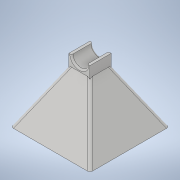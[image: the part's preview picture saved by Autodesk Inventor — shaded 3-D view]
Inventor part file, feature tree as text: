
AUTODESK INVENTOR PART (.ipt)
format: ipt  version: 2022.1 (Build 261234020, 234B)  size: 131,072 bytes
history: native  units: in
note: dims shown in document units (in); Inventor stores cm internally (conversion verified against a paired STEP export)
features: sketch x3, plane x2, fillet x2, loft x1, extrude x1
ambient origin geometry x8: Origin, YZ Plane, XZ Plane, XY Plane, X Axis, Y Axis, Z Axis, Center Point
bodies: Solid1 (feature_tree)
feature tree (9):
  sketch  "Sketch1"  dims[d3=0.0in d4=90.0deg d5=0.0in d6=90.0deg]
  plane  "Work Plane1"
  loft  "Loft1"
  extrude  "Extrusion1"  Depth=0.0625in
  fillet  "Fillet3"  Radius=0.0312in
  fillet  "Fillet5"  Radius=0.75in
  plane  "Work Plane2"
  sketch  "Sketch2"  dims[d11=0.0in d14=0.0625in d16=0.0312in d17=0.75in]
  sketch  "Sketch3"
